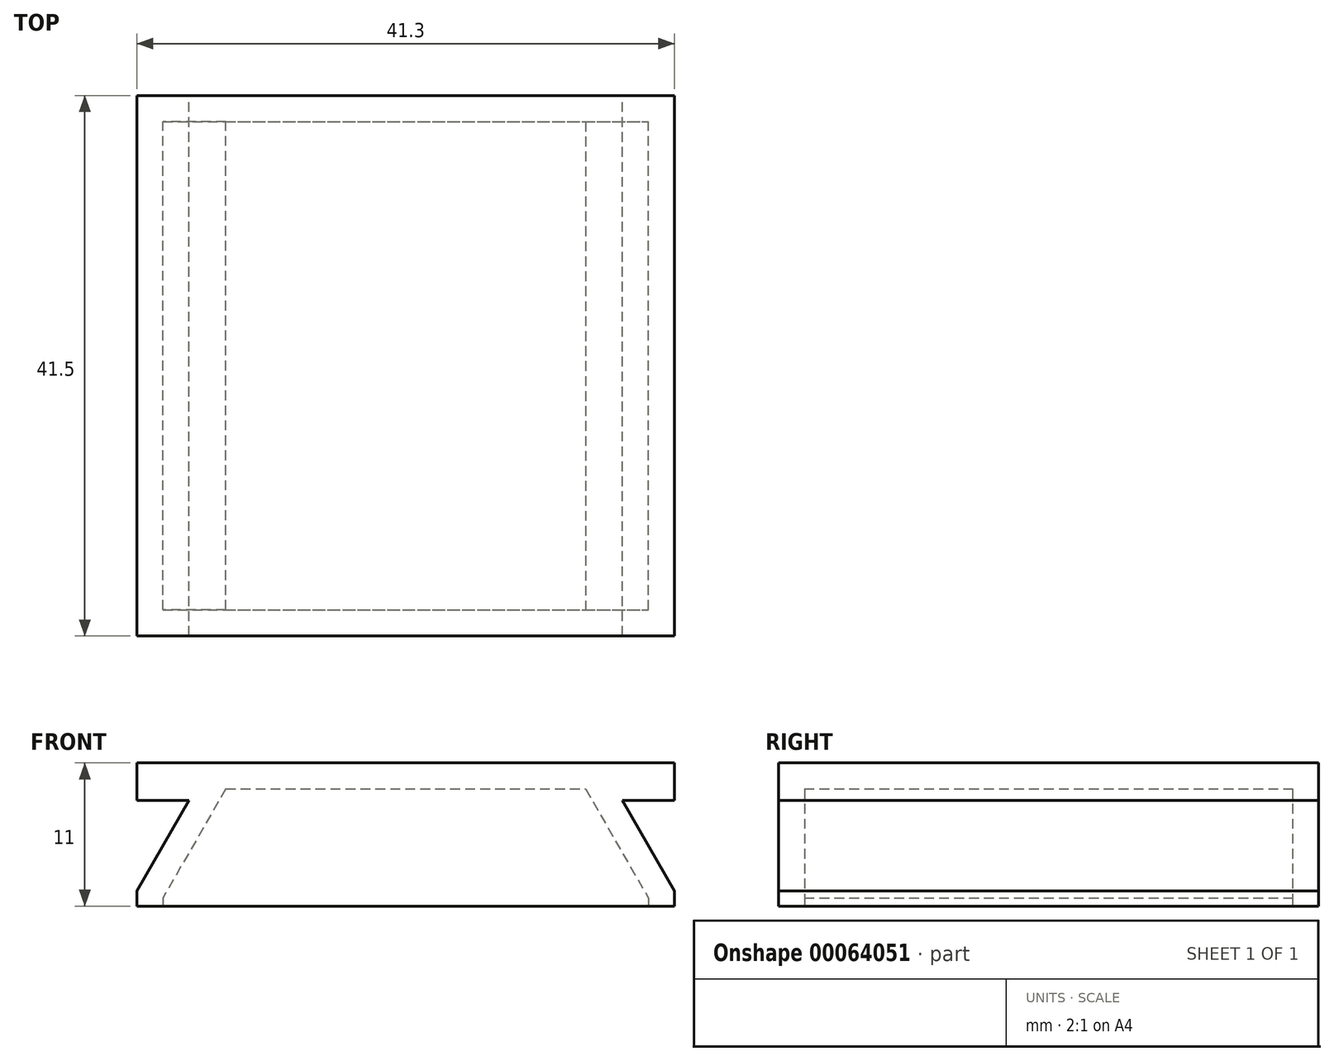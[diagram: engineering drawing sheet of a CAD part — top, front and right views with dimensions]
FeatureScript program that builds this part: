
annotation { "Feature Type Name" : "Feature", "Feature Type Description" : "" }
export const myFeature = defineFeature(function(context is Context, id is Id, definition is map)
    precondition{}
    {
        {
            var Q0;
            Q0=qCreatedBy(makeId("Front.planeOp"),FACE);
            var sketch = newSketch(context, id + "F0", { "sketchPlane" : qUnion([Q0])});
            skLineSegment(sketch, "E0.bottom", {"start": v(-20.65, 0) * mm, "end": v(20.65, 0) * mm});
            skLineSegment(sketch, "E0.top", {"start": v(-20.65, -11) * mm, "end": v(20.65, -11) * mm});
            skLineSegment(sketch, "E0.left", {"start": v(-20.65, 0) * mm, "end": v(-20.65, -11) * mm, "construction": true});
            skLineSegment(sketch, "E0.right", {"start": v(20.65, 0) * mm, "end": v(20.65, -11) * mm, "construction": true});
            skLineSegment(sketch, "E1", {"start": v(-20.65, 0) * mm, "end": v(-20.65, -2.9) * mm});
            skLineSegment(sketch, "E2", {"start": v(-20.65, -2.9) * mm, "end": v(-16.65, -2.9) * mm});
            skLineSegment(sketch, "E3", {"start": v(-16.65, -2.9) * mm, "end": v(-20.65, -9.83) * mm});
            skLineSegment(sketch, "E4", {"start": v(-20.65, -9.83) * mm, "end": v(-20.65, -11) * mm});
            skLineSegment(sketch, "E5.MirrorCS", {"start": v(16.65, -2.9) * mm, "end": v(20.65, -9.83) * mm});
            skLineSegment(sketch, "E6.MirrorCS", {"start": v(20.65, -9.83) * mm, "end": v(20.65, -11) * mm});
            skLineSegment(sketch, "E7.MirrorCS", {"start": v(20.65, -2.9) * mm, "end": v(16.65, -2.9) * mm});
            skLineSegment(sketch, "E8.MirrorCS", {"start": v(20.65, 0) * mm, "end": v(20.65, -2.9) * mm});
            skSolve(sketch);
        }
        {
            var Q0;
            Q0 = qSketchRegion(id + "F0", true);
            extrude(context, id + "F1", {"entities" : qUnion([Q0]), "endBound" : BoundingType.SYMMETRIC, "depth" : 41.5 * mm});
        }
        {
            var Q0;
            Q0=makeQuery(id+"F1.opExtrude","SWEPT_FACE",FACE,{"disambiguationData":[OSD([sQuery(id+"F0.wireOp",EDGE,"E0.top")])]});
            shell(context, id + "F2", {"entities" : qUnion([Q0]), "thickness" : 2 * mm});
        }
    });
